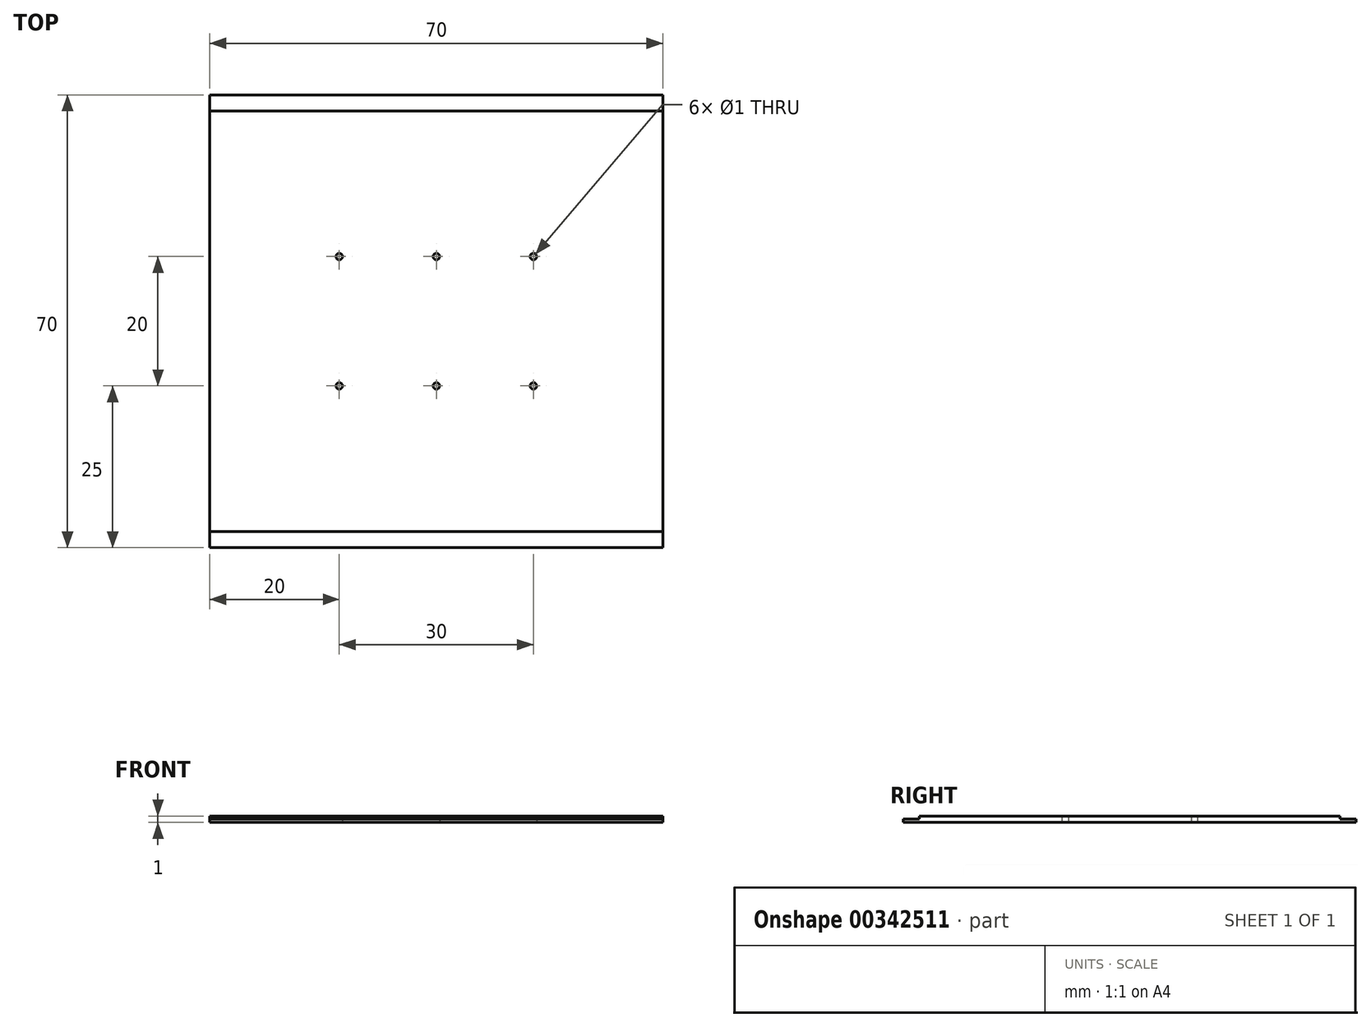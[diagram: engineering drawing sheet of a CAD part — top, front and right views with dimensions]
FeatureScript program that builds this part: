
annotation { "Feature Type Name" : "Feature", "Feature Type Description" : "" }
export const myFeature = defineFeature(function(context is Context, id is Id, definition is map)
    precondition{}
    {
        {
            var Q0;
            Q0=qCreatedBy(makeId("Top.planeOp"),FACE);
            var sketch = newSketch(context, id + "F0", { "sketchPlane" : qUnion([Q0])});
            skLineSegment(sketch, "E0.bottom", {"start": v(35, 32.5) * mm, "end": v(-35, 32.5) * mm});
            skLineSegment(sketch, "E0.top", {"start": v(35, -32.5) * mm, "end": v(-35, -32.5) * mm});
            skLineSegment(sketch, "E0.left", {"start": v(35, 32.5) * mm, "end": v(35, -32.5) * mm});
            skLineSegment(sketch, "E0.right", {"start": v(-35, 32.5) * mm, "end": v(-35, -32.5) * mm});
            skPoint(sketch, "E0.middle", {"position": v(0, 0) * mm});
            skLineSegment(sketch, "E1.bottom", {"start": v(35, 35) * mm, "end": v(-35, 35) * mm});
            skLineSegment(sketch, "E1.top", {"start": v(35, -35) * mm, "end": v(-35, -35) * mm});
            skLineSegment(sketch, "E1.left", {"start": v(35, 35) * mm, "end": v(35, -35) * mm});
            skLineSegment(sketch, "E1.right", {"start": v(-35, 35) * mm, "end": v(-35, -35) * mm});
            skLineSegment(sketch, "E2.bottom", {"start": v(15, 10) * mm, "end": v(-15, 10) * mm, "construction": true});
            skLineSegment(sketch, "E2.top", {"start": v(15, -10) * mm, "end": v(-15, -10) * mm, "construction": true});
            skLineSegment(sketch, "E2.left", {"start": v(15, 10) * mm, "end": v(15, -10) * mm, "construction": true});
            skLineSegment(sketch, "E2.right", {"start": v(-15, 10) * mm, "end": v(-15, -10) * mm, "construction": true});
            skCircle(sketch, "E3", {"center": v(-15, -10) * mm, "radius": 0.5 * mm});
            skCircle(sketch, "E4.0.1.0", {"center": v(-15, 10) * mm, "radius": 0.5 * mm});
            skCircle(sketch, "E4.1.0.0", {"center": v(0, -10) * mm, "radius": 0.5 * mm});
            skCircle(sketch, "E4.1.1.0", {"center": v(0, 10) * mm, "radius": 0.5 * mm});
            skCircle(sketch, "E4.2.0.0", {"center": v(15, -10) * mm, "radius": 0.5 * mm});
            skCircle(sketch, "E4.2.1.0", {"center": v(15, 10) * mm, "radius": 0.5 * mm});
            skLineSegment(sketch, "E4.direction1", {"start": v(-15, -10) * mm, "end": v(0, -10) * mm, "construction": true});
            skLineSegment(sketch, "E4.direction2", {"start": v(-15, -10) * mm, "end": v(-15, 10) * mm, "construction": true});
            skSolve(sketch);
        }
        {
            var Q0;
            {var subQ1=sQuery(id+"F0.wireOp",EDGE,"E0.bottom");Q0=makeQuery(id+"F0.imprint","IMPRINT",FACE,{"disambiguationData":[TD([[makeQuery(id+"F0.imprint","IMPRINT",EDGE,{"derivedFrom":subQ1}),1.0]])]});}
            extrude(context, id + "F1", {"entities" : qUnion([Q0]), "depth" : 1 * mm});
        }
        {
            var Q0;
            Q0 = qSketchRegion(id + "F0", true);
            extrude(context, id + "F2", {"entities" : qUnion([Q0]), "operationType" : NewBodyOperationType.ADD, "depth" : .5 * mm});
        }
    });
